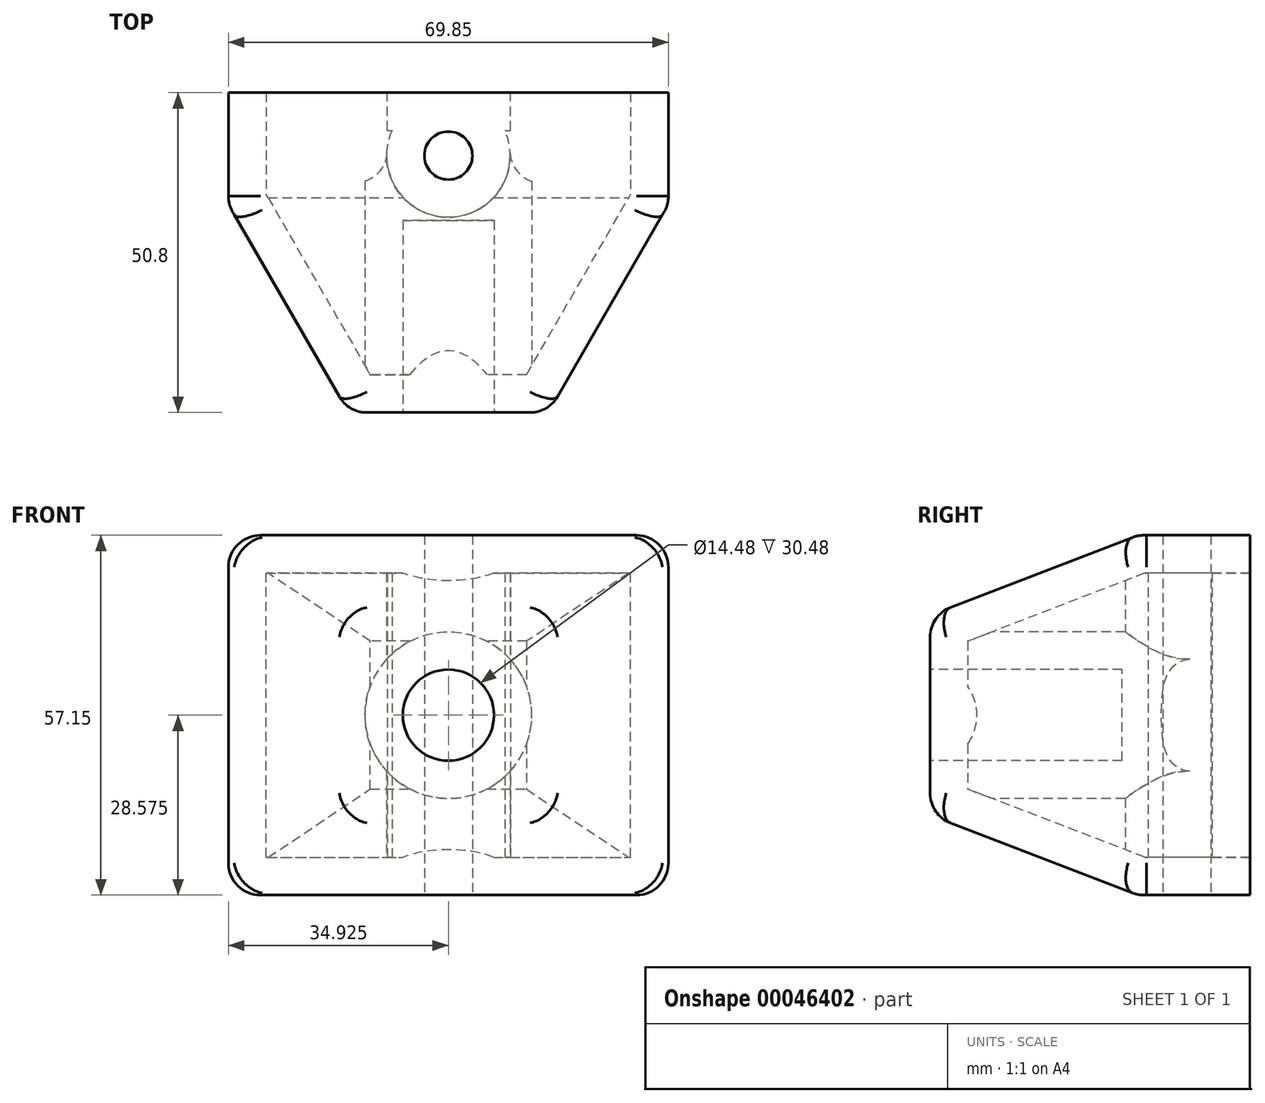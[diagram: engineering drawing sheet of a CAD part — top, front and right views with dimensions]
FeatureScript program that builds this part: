
annotation { "Feature Type Name" : "Feature", "Feature Type Description" : "" }
export const myFeature = defineFeature(function(context is Context, id is Id, definition is map)
    precondition{}
    {
        {
            var Q0;
            Q0=qCreatedBy(makeId("Front.planeOp"),FACE);
            var sketch = newSketch(context, id + "F0", { "sketchPlane" : qUnion([Q0])});
            skLineSegment(sketch, "E0.bottom", {"start": v(0, 0) * mm, "end": v(69.85, 0) * mm});
            skLineSegment(sketch, "E0.top", {"start": v(0, 57.15) * mm, "end": v(69.85, 57.15) * mm});
            skLineSegment(sketch, "E0.left", {"start": v(0, 0) * mm, "end": v(0, 57.15) * mm});
            skLineSegment(sketch, "E0.right", {"start": v(69.85, 0) * mm, "end": v(69.85, 57.15) * mm});
            skSolve(sketch);
        }
        {
            var Q0;
            Q0=makeQuery(id+"F0.imprint","IMPRINT",FACE,{"disambiguationData":[TD([[makeQuery(id+"F0.imprint","IMPRINT",EDGE,{"derivedFrom":sQuery(id+"F0.wireOp",EDGE,"E0.bottom")}),1.0]])]});
            extrude(context, id + "F1", {"entities" : qUnion([Q0]), "depth" : 50.8 * mm});
        }
        {
            var Q0;
            Q0=makeQuery(id+"F1.opExtrude","CAP_FACE",FACE,{"disambiguationData":[OSD([sQuery(id+"F0.wireOp",EDGE,"E0.bottom"),sQuery(id+"F0.wireOp",EDGE,"E0.top"),sQuery(id+"F0.wireOp",EDGE,"E0.left"),sQuery(id+"F0.wireOp",EDGE,"E0.right")])],"isStart":false});
            var sketch = newSketch(context, id + "F2", { "sketchPlane" : qUnion([Q0])});
            skCircle(sketch, "E1", {"center": v(34.93, 28.58) * mm, "radius": 7.24 * mm});
            skPoint(sketch, "E1.centerSnap0", {"position": v(34.93, 0) * mm});
            skSolve(sketch);
        }
        {
            var Q0;
            Q0=makeQuery(id+"F2.imprint","IMPRINT",FACE,{"disambiguationData":[TD([[makeQuery(id+"F2.imprint","IMPRINT",EDGE,{"derivedFrom":sQuery(id+"F2.wireOp",EDGE,"E1")}),1.0]])]});
            extrude(context, id + "F3", {"entities" : qUnion([Q0]), "operationType" : NewBodyOperationType.REMOVE, "oppositeDirection" : true, "depth" : 30.48 * mm});
        }
        {
            var Q0;
            Q0=makeQuery(id+"F1.opExtrude","SWEPT_FACE",FACE,{"disambiguationData":[OSD([sQuery(id+"F0.wireOp",EDGE,"E0.bottom")])]});
            var sketch = newSketch(context, id + "F4", { "sketchPlane" : qUnion([Q0])});
            skCircle(sketch, "E2", {"center": v(34.93, 10) * mm, "radius": 3.81 * mm});
            skPoint(sketch, "E2.centerSnap0", {"position": v(34.93, 0) * mm});
            skSolve(sketch);
        }
        {
            var Q0;
            Q0=makeQuery(id+"F1.opExtrude","CAP_EDGE",EDGE,{"disambiguationData":[OSD([sQuery(id+"F0.wireOp",EDGE,"E0.top")])],"isStart":false});
            var Q1;
            Q1=makeQuery(id+"F1.opExtrude","CAP_EDGE",EDGE,{"disambiguationData":[OSD([sQuery(id+"F0.wireOp",EDGE,"E0.bottom")])],"isStart":false});
            chamfer(context, id + "F5", {"entities" : qUnion([Q0, Q1]), "chamferType" : ChamferType.TWO_OFFSETS, "width1" : 33.02 * mm, "oppositeDirection" : false, "width2" : 12.7 * mm, "tangentPropagation" : true});
        }
        {
            var Q0;
            Q0=makeQuery(id+"F1.opExtrude","CAP_EDGE",EDGE,{"disambiguationData":[OSD([sQuery(id+"F0.wireOp",EDGE,"E0.right")])],"isStart":false});
            var Q1;
            Q1=makeQuery(id+"F1.opExtrude","CAP_EDGE",EDGE,{"disambiguationData":[OSD([sQuery(id+"F0.wireOp",EDGE,"E0.left")])],"isStart":false});
            chamfer(context, id + "F6", {"entities" : qUnion([Q0, Q1]), "chamferType" : ChamferType.TWO_OFFSETS, "width1" : 19.05 * mm, "oppositeDirection" : false, "width2" : 33.02 * mm, "tangentPropagation" : true});
        }
        {
            var Q0;
            Q0=makeQuery(id+"F4.imprint","IMPRINT",FACE,{"disambiguationData":[TD([[makeQuery(id+"F4.imprint","IMPRINT",EDGE,{"derivedFrom":sQuery(id+"F4.wireOp",EDGE,"E2")}),1.0]])]});
            extrude(context, id + "F7", {"entities" : qUnion([Q0]), "operationType" : NewBodyOperationType.REMOVE, "oppositeDirection" : true, "depth" : 76.2 * mm});
        }
        {
            var Q0;
            Q0=makeQuery(id+"F1.opExtrude","SWEPT_EDGE",EDGE,{"disambiguationData":[OSD([sQuery(id+"F0.wireOp",EDGE,"E0.top"),sQuery(id+"F0.wireOp",EDGE,"E0.left")])]});
            var Q1;
            Q1=makeQuery(id+"F1.opExtrude","SWEPT_EDGE",EDGE,{"disambiguationData":[OSD([sQuery(id+"F0.wireOp",EDGE,"E0.bottom"),sQuery(id+"F0.wireOp",EDGE,"E0.left")])]});
            var Q2;
            Q2=makeQuery(id+"F1.opExtrude","SWEPT_EDGE",EDGE,{"disambiguationData":[OSD([sQuery(id+"F0.wireOp",EDGE,"E0.top"),sQuery(id+"F0.wireOp",EDGE,"E0.right")])]});
            var Q3;
            Q3=makeQuery(id+"F1.opExtrude","SWEPT_EDGE",EDGE,{"disambiguationData":[OSD([sQuery(id+"F0.wireOp",EDGE,"E0.bottom"),sQuery(id+"F0.wireOp",EDGE,"E0.right")])]});
            fillet(context, id + "F8", {"entities" : qUnion([Q0, Q1, Q2, Q3]), "radius" : 5.08 * mm, "tangentPropagation" : true, "allowEdgeOverflow" : false});
        }
        {
            var Q0;
            Q0=makeQuery(id+"F6.opChamfer","BLEND_EDGE",EDGE,{"blendedFrom":[makeQuery(id+"F1.opExtrude","CAP_EDGE",EDGE,{"disambiguationData":[OSD([sQuery(id+"F0.wireOp",EDGE,"E0.right")])],"isStart":false}),makeQuery(id+"F5.opChamfer","BLEND_FACE",FACE,{"disambiguationData":[OSD([sQuery(id+"F0.wireOp",EDGE,"E0.top")])]})],"blendedInto":[makeQuery(id+"F5.opChamfer","BLEND_FACE",FACE,{"disambiguationData":[OSD([sQuery(id+"F0.wireOp",EDGE,"E0.top")])]})]});
            var Q1;
            Q1=makeQuery(id+"F6.opChamfer","BLEND_EDGE",EDGE,{"blendedFrom":[makeQuery(id+"F1.opExtrude","CAP_EDGE",EDGE,{"disambiguationData":[OSD([sQuery(id+"F0.wireOp",EDGE,"E0.right")])],"isStart":false}),makeQuery(id+"F5.opChamfer","BLEND_FACE",FACE,{"disambiguationData":[OSD([sQuery(id+"F0.wireOp",EDGE,"E0.bottom")])]})],"blendedInto":[makeQuery(id+"F5.opChamfer","BLEND_FACE",FACE,{"disambiguationData":[OSD([sQuery(id+"F0.wireOp",EDGE,"E0.bottom")])]})]});
            var Q2;
            Q2=makeQuery(id+"F6.opChamfer","BLEND_EDGE",EDGE,{"blendedFrom":[makeQuery(id+"F1.opExtrude","CAP_EDGE",EDGE,{"disambiguationData":[OSD([sQuery(id+"F0.wireOp",EDGE,"E0.left")])],"isStart":false}),makeQuery(id+"F5.opChamfer","BLEND_FACE",FACE,{"disambiguationData":[OSD([sQuery(id+"F0.wireOp",EDGE,"E0.bottom")])]})],"blendedInto":[makeQuery(id+"F5.opChamfer","BLEND_FACE",FACE,{"disambiguationData":[OSD([sQuery(id+"F0.wireOp",EDGE,"E0.bottom")])]})]});
            var Q3;
            Q3=makeQuery(id+"F6.opChamfer","BLEND_EDGE",EDGE,{"blendedFrom":[makeQuery(id+"F1.opExtrude","CAP_EDGE",EDGE,{"disambiguationData":[OSD([sQuery(id+"F0.wireOp",EDGE,"E0.left")])],"isStart":false}),makeQuery(id+"F5.opChamfer","BLEND_FACE",FACE,{"disambiguationData":[OSD([sQuery(id+"F0.wireOp",EDGE,"E0.top")])]})],"blendedInto":[makeQuery(id+"F5.opChamfer","BLEND_FACE",FACE,{"disambiguationData":[OSD([sQuery(id+"F0.wireOp",EDGE,"E0.top")])]})]});
            fillet(context, id + "F9", {"entities" : qUnion([Q0, Q1, Q2, Q3]), "radius" : 5.08 * mm, "tangentPropagation" : true, "allowEdgeOverflow" : false});
        }
        {
            var Q0;
            {var subQ0=sQuery(id+"F0.wireOp",EDGE,"E0.left");Q0=makeQuery(id+"F6.opChamfer","BLEND_EDGE",EDGE,{"blendedFrom":[makeQuery(id+"F1.opExtrude","CAP_EDGE",EDGE,{"disambiguationData":[OSD([subQ0])],"isStart":false}),makeQuery(id+"F1.opExtrude","CAP_FACE",FACE,{"disambiguationData":[OSD([sQuery(id+"F0.wireOp",EDGE,"E0.bottom"),sQuery(id+"F0.wireOp",EDGE,"E0.top"),subQ0,sQuery(id+"F0.wireOp",EDGE,"E0.right")])],"isStart":false})],"blendedInto":[makeQuery(id+"F1.opExtrude","CAP_FACE",FACE,{"disambiguationData":[OSD([sQuery(id+"F0.wireOp",EDGE,"E0.bottom"),sQuery(id+"F0.wireOp",EDGE,"E0.top"),subQ0,sQuery(id+"F0.wireOp",EDGE,"E0.right")])],"isStart":false})]});}
            fillet(context, id + "F10", {"entities" : qUnion([Q0]), "radius" : 5.08 * mm, "tangentPropagation" : true, "allowEdgeOverflow" : false});
        }
        {
            var Q0;
            {var subQ0=sQuery(id+"F0.wireOp",EDGE,"E0.left");Q0=makeQuery(id+"F6.opChamfer","BLEND_EDGE",EDGE,{"blendedFrom":[makeQuery(id+"F1.opExtrude","CAP_EDGE",EDGE,{"disambiguationData":[OSD([subQ0])],"isStart":false}),makeQuery(id+"F1.opExtrude","SWEPT_FACE",FACE,{"disambiguationData":[OSD([subQ0])]})],"blendedInto":[makeQuery(id+"F1.opExtrude","SWEPT_FACE",FACE,{"disambiguationData":[OSD([subQ0])]})]});}
            fillet(context, id + "F11", {"entities" : qUnion([Q0]), "radius" : 5.08 * mm, "tangentPropagation" : true, "allowEdgeOverflow" : false});
        }
        {
            var Q0;
            Q0=makeQuery(id+"F1.opExtrude","CAP_FACE",FACE,{"disambiguationData":[OSD([sQuery(id+"F0.wireOp",EDGE,"E0.bottom"),sQuery(id+"F0.wireOp",EDGE,"E0.top"),sQuery(id+"F0.wireOp",EDGE,"E0.left"),sQuery(id+"F0.wireOp",EDGE,"E0.right")])],"isStart":true});
            shell(context, id + "F12", {"entities" : qUnion([Q0]), "thickness" : 6 * mm});
        }
        {
            var Q0;
            Q0=makeQuery(id+"F12.opShell","TWEAK_EDGE",EDGE,{"disambiguationData":[OD(0.0)],"derivedFrom":[makeQuery(id+"F3.boolean.opBoolean","COPY",FACE,{"derivedFrom":makeQuery(id+"F3.opExtrude","CAP_FACE",FACE,{"disambiguationData":[OSD([sQuery(id+"F2.wireOp",EDGE,"E1")])],"isStart":false})}),makeQuery(id+"F7.boolean.opBoolean","COPY",FACE,{"derivedFrom":makeQuery(id+"F7.opExtrude","SWEPT_FACE",FACE,{"disambiguationData":[OSD([sQuery(id+"F4.wireOp",EDGE,"E2")])]})})]});
            var Q1;
            Q1=makeQuery(id+"F12.opShell","TWEAK_EDGE",EDGE,{"disambiguationData":[OD(1.0)],"derivedFrom":[makeQuery(id+"F3.boolean.opBoolean","COPY",FACE,{"derivedFrom":makeQuery(id+"F3.opExtrude","CAP_FACE",FACE,{"disambiguationData":[OSD([sQuery(id+"F2.wireOp",EDGE,"E1")])],"isStart":false})}),makeQuery(id+"F7.boolean.opBoolean","COPY",FACE,{"derivedFrom":makeQuery(id+"F7.opExtrude","SWEPT_FACE",FACE,{"disambiguationData":[OSD([sQuery(id+"F4.wireOp",EDGE,"E2")])]})})]});
            fillet(context, id + "F13", {"entities" : qUnion([Q0, Q1]), "radius" : 5 * mm, "tangentPropagation" : true, "allowEdgeOverflow" : false});
        }
        {
            var Q0;
            Q0=makeQuery(id+"F0.imprint","IMPRINT",FACE,{"disambiguationData":[TD([[makeQuery(id+"F0.imprint","IMPRINT",EDGE,{"derivedFrom":sQuery(id+"F0.wireOp",EDGE,"E0.bottom")}),1.0]])]});
            var sketch = newSketch(context, id + "F14", { "sketchPlane" : qUnion([Q0])});
            skLineSegment(sketch, "E3.bottom", {"start": v(44.8, 53.83) * mm, "end": v(25.21, 53.83) * mm});
            skLineSegment(sketch, "E3.top", {"start": v(44.8, 3.25) * mm, "end": v(25.21, 3.25) * mm});
            skLineSegment(sketch, "E3.left", {"start": v(44.8, 53.83) * mm, "end": v(44.8, 3.25) * mm});
            skLineSegment(sketch, "E3.right", {"start": v(25.21, 53.83) * mm, "end": v(25.21, 3.25) * mm});
            skSolve(sketch);
        }
        {
            var Q0;
            Q0 = qSketchRegion(id + "F14", true);
            extrude(context, id + "F15", {"entities" : qUnion([Q0]), "operationType" : NewBodyOperationType.ADD, "depth" : 6 * mm});
        }
    });
